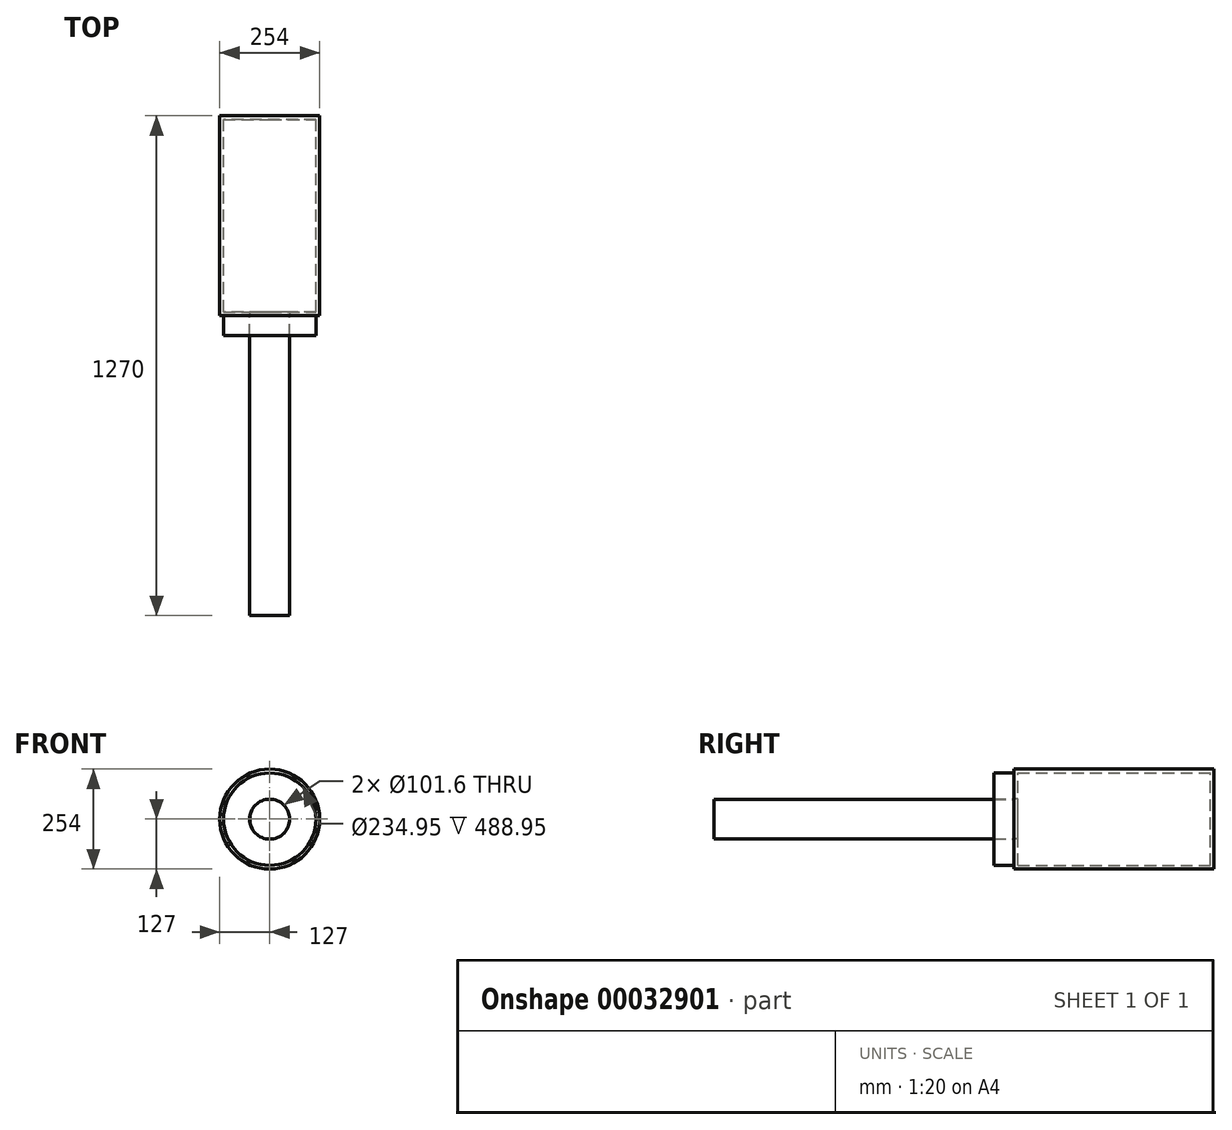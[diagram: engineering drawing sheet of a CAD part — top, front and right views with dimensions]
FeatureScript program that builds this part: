
annotation { "Feature Type Name" : "Feature", "Feature Type Description" : "" }
export const myFeature = defineFeature(function(context is Context, id is Id, definition is map)
    precondition{}
    {
        {
            var Q0;
            Q0=qCreatedBy(makeId("Front.planeOp"),FACE);
            var sketch = newSketch(context, id + "F0", { "sketchPlane" : qUnion([Q0])});
            skCircle(sketch, "E0", {"center": v(0, 0) * mm, "radius": 127 * mm});
            skSolve(sketch);
        }
        {
            var Q0;
            Q0=makeQuery(id+"F0.imprint","IMPRINT",FACE,{"disambiguationData":[TD([[makeQuery(id+"F0.imprint","IMPRINT",EDGE,{"derivedFrom":sQuery(id+"F0.wireOp",EDGE,"E0")}),1.0]])]});
            extrude(context, id + "F1", {"entities" : qUnion([Q0]), "endBound" : BoundingType.SYMMETRIC, "depth" : 508 * mm});
        }
        {
            var Q0;
            Q0=makeQuery(id+"F1.opExtrude","CAP_FACE",FACE,{"disambiguationData":[OSD([sQuery(id+"F0.wireOp",EDGE,"E0")])],"isStart":false});
            var Q1;
            Q1=makeQuery(id+"F1.opExtrude","SWEPT_BODY",BODY,{"disambiguationData":[OSD([sQuery(id+"F0.wireOp",EDGE,"E0")])]});
            shell(context, id + "F2", {"isHollow" : true, "entities" : qUnion([Q0]), "parts" : qUnion([Q1]), "thickness" : 9.52 * mm});
        }
        {
            var Q0;
            Q0=makeQuery(id+"F1.opExtrude","CAP_FACE",FACE,{"disambiguationData":[OSD([sQuery(id+"F0.wireOp",EDGE,"E0")])],"isStart":false});
            var sketch = newSketch(context, id + "F3", { "sketchPlane" : qUnion([Q0])});
            skCircle(sketch, "E1.0.0", {"center": v(0, 0) * mm, "radius": 127 * mm});
            skCircle(sketch, "E2", {"center": v(0, 0) * mm, "radius": 50.8 * mm});
            skSolve(sketch);
        }
        {
            var Q0;
            Q0=makeQuery(id+"F3.imprint","IMPRINT",FACE,{"disambiguationData":[TD([[makeQuery(id+"F3.imprint","IMPRINT",EDGE,{"derivedFrom":sQuery(id+"F3.wireOp",EDGE,"E2")}),1.0]])]});
            extrude(context, id + "F4", {"entities" : qUnion([Q0]), "operationType" : NewBodyOperationType.REMOVE, "endBound" : BoundingType.UP_TO_NEXT, "oppositeDirection" : true, "depth" : 25.4 * mm});
        }
        {
            var Q0;
            Q0=makeQuery(id+"F1.opExtrude","CAP_FACE",FACE,{"disambiguationData":[OSD([sQuery(id+"F0.wireOp",EDGE,"E0")])],"isStart":false});
            var sketch = newSketch(context, id + "F5", { "sketchPlane" : qUnion([Q0])});
            skCircle(sketch, "E3.0", {"center": v(0, 0) * mm, "radius": 50.8 * mm});
            skCircle(sketch, "E4", {"center": v(0, 0) * mm, "radius": 50.67 * mm});
            skSolve(sketch);
        }
        {
            var Q0;
            Q0=makeQuery(id+"F5.imprint","IMPRINT",FACE,{"disambiguationData":[TD([[makeQuery(id+"F5.imprint","IMPRINT",EDGE,{"derivedFrom":sQuery(id+"F5.wireOp",EDGE,"E4")}),1.0]])]});
            extrude(context, id + "F6", {"entities" : qUnion([Q0]), "depth" : 762 * mm});
        }
        {
            var Q0;
            Q0=makeQuery(id+"F1.opExtrude","CAP_FACE",FACE,{"disambiguationData":[OSD([sQuery(id+"F0.wireOp",EDGE,"E0")])],"isStart":false});
            var sketch = newSketch(context, id + "F7", { "sketchPlane" : qUnion([Q0])});
            skCircle(sketch, "E5", {"center": v(0, 0) * mm, "radius": 117.35 * mm});
            skSolve(sketch);
        }
        {
            var Q0;
            Q0=makeQuery(id+"F7.imprint","IMPRINT",FACE,{"disambiguationData":[TD([[makeQuery(id+"F7.imprint","IMPRINT",EDGE,{"derivedFrom":sQuery(id+"F7.wireOp",EDGE,"E5")}),1.0]])]});
            extrude(context, id + "F8", {"entities" : qUnion([Q0]), "depth" : 50.8 * mm});
        }
    });
